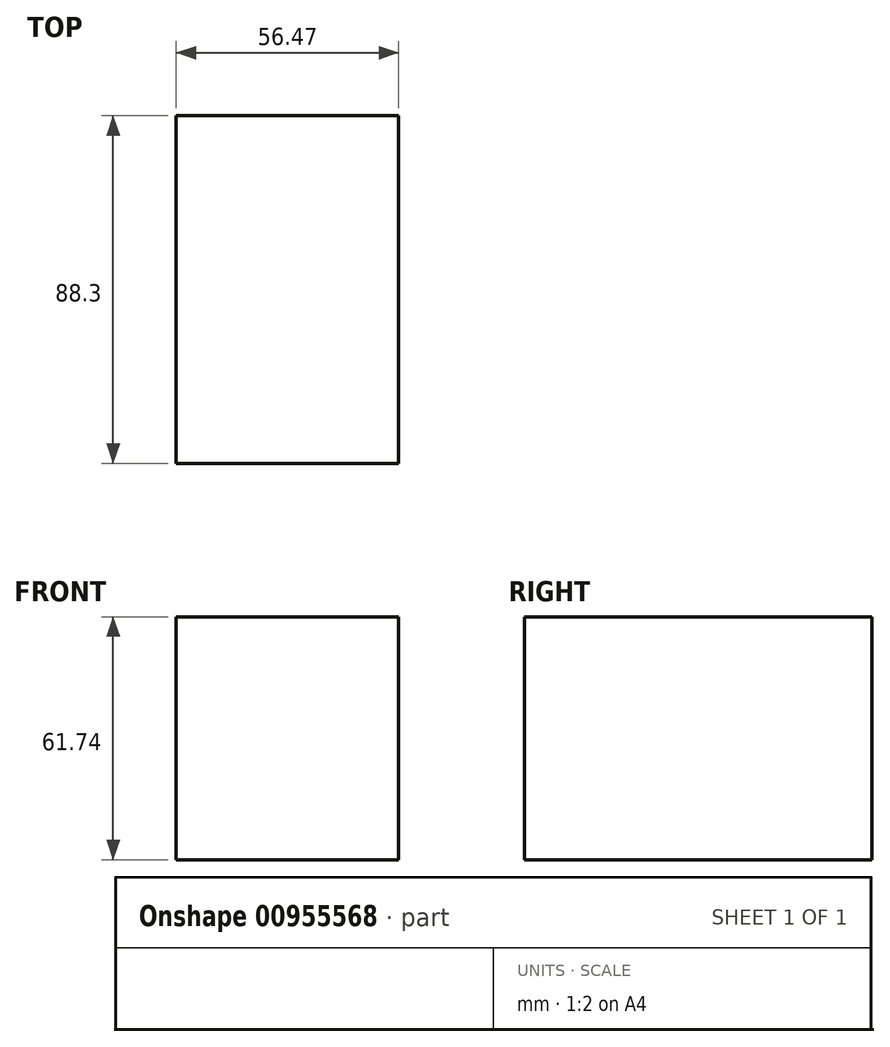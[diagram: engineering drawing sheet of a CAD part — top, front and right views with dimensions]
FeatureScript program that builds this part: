
annotation { "Feature Type Name" : "Feature", "Feature Type Description" : "" }
export const myFeature = defineFeature(function(context is Context, id is Id, definition is map)
    precondition{}
    {
        {
            var Q0;
            Q0=qCreatedBy(makeId("Front.planeOp"),FACE);
            var sketch = newSketch(context, id + "F0", { "sketchPlane" : qUnion([Q0])});
            skLineSegment(sketch, "E0.bottom", {"start": v(-112.46, 4.7) * mm, "end": v(-55.99, 4.7) * mm});
            skLineSegment(sketch, "E0.top", {"start": v(-112.46, 66.44) * mm, "end": v(-55.99, 66.44) * mm});
            skLineSegment(sketch, "E0.left", {"start": v(-112.46, 4.7) * mm, "end": v(-112.46, 66.44) * mm});
            skLineSegment(sketch, "E0.right", {"start": v(-55.99, 4.7) * mm, "end": v(-55.99, 66.44) * mm});
            skPoint(sketch, "E0.middle", {"position": v(-84.22, 35.57) * mm});
            skSolve(sketch);
        }
        {
            var Q0;
            Q0=makeQuery(id+"F0.imprint","IMPRINT",FACE,{"disambiguationData":[TD([[makeQuery(id+"F0.imprint","IMPRINT",EDGE,{"derivedFrom":sQuery(id+"F0.wireOp",EDGE,"E0.bottom")}),1.0]])]});
            extrude(context, id + "F1", {"entities" : qUnion([Q0]), "depth" : 88.3 * mm, "offsetDistance" : 25 * mm});
        }
    });
